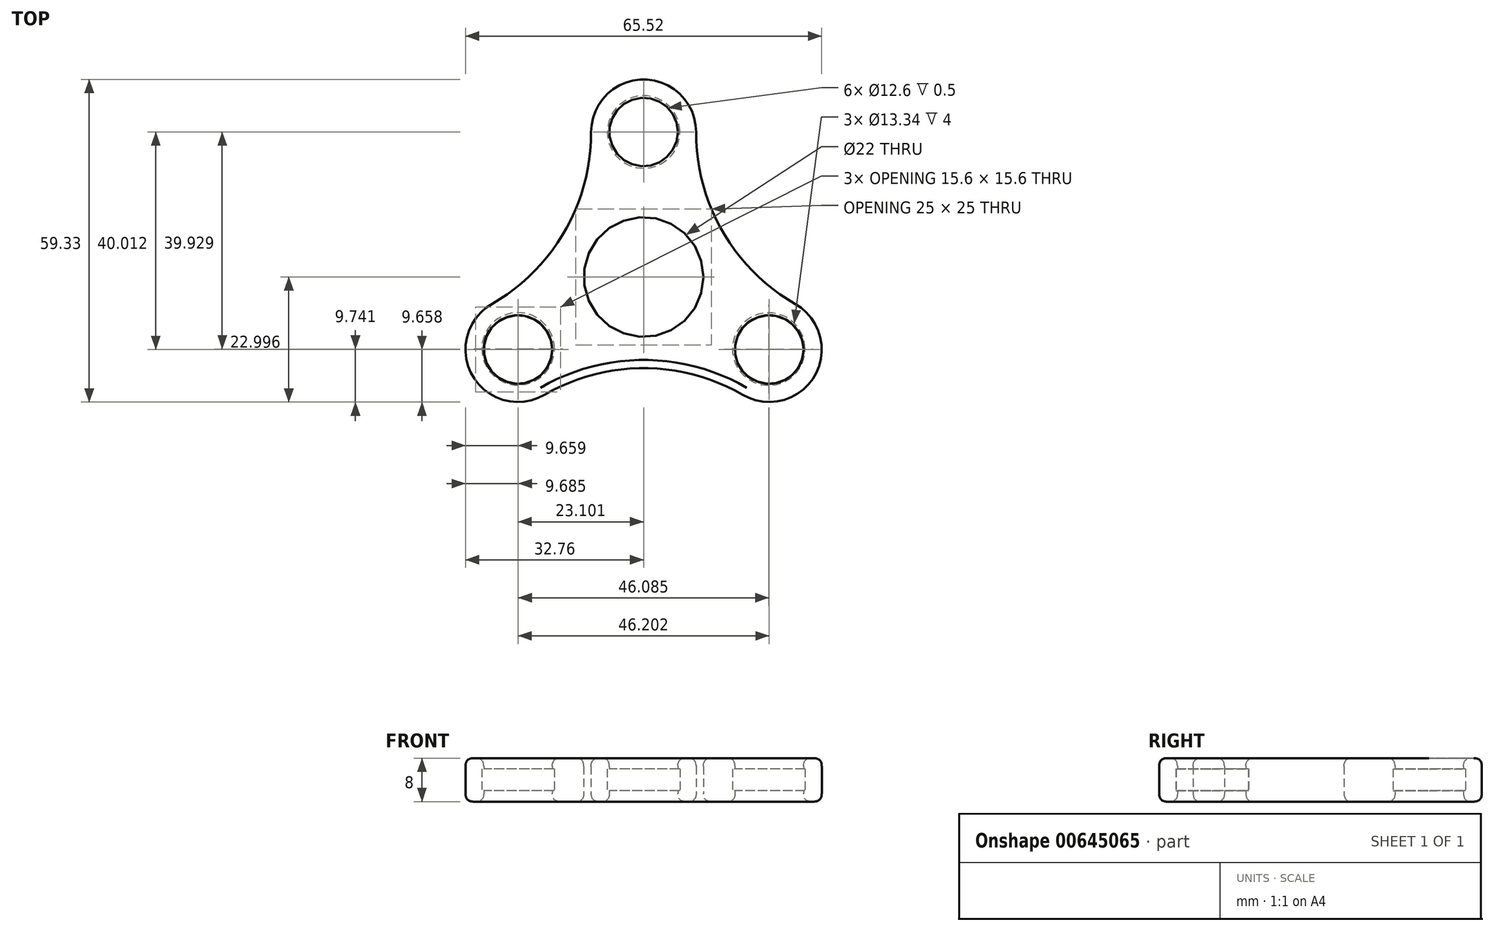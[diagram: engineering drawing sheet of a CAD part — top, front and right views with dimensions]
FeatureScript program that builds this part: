
annotation { "Feature Type Name" : "Feature", "Feature Type Description" : "" }
export const myFeature = defineFeature(function(context is Context, id is Id, definition is map)
    precondition{}
    {
        {
            var Q0;
            Q0=qCreatedBy(makeId("Top.planeOp"),FACE);
            var sketch = newSketch(context, id + "F0", { "sketchPlane" : qUnion([Q0])});
            skCircle(sketch, "E0", {"center": v(0, 0) * mm, "radius": 6.3 * mm});
            skCircle(sketch, "E1", {"center": v(0, 0) * mm, "radius": 9.66 * mm});
            skCircle(sketch, "E2.1.0", {"center": v(-23.1, -40.01) * mm, "radius": 9.66 * mm});
            skCircle(sketch, "E2.1.1", {"center": v(-23.1, -40.01) * mm, "radius": 6.3 * mm});
            skCircle(sketch, "E2.2.0", {"center": v(23.1, -40.01) * mm, "radius": 9.66 * mm});
            skCircle(sketch, "E2.2.1", {"center": v(23.1, -40.01) * mm, "radius": 6.3 * mm});
            skPoint(sketch, "E2.center", {"position": v(0, -26.67) * mm});
            skLineSegment(sketch, "E3", {"start": v(0, 0) * mm, "end": v(-9.66, 0) * mm, "construction": true});
            skCircle(sketch, "E4", {"center": v(0, -26.67) * mm, "radius": 11 * mm});
            skLineSegment(sketch, "E5", {"start": v(0, -26.67) * mm, "end": v(-23.1, -40.01) * mm, "construction": true});
            skLineSegment(sketch, "E6", {"start": v(23.1, -40.01) * mm, "end": v(0, -26.67) * mm, "construction": true});
            skLineSegment(sketch, "E7", {"start": v(0, -26.67) * mm, "end": v(0, 0) * mm, "construction": true});
            skLineSegment(sketch, "E8", {"start": v(23.1, -40.01) * mm, "end": v(27.93, -31.64) * mm, "construction": true});
            skLineSegment(sketch, "E9", {"start": v(0, 0) * mm, "end": v(9.66, 0) * mm, "construction": true});
            skLineSegment(sketch, "E10", {"start": v(-23.1, -40.01) * mm, "end": v(-27.93, -31.64) * mm, "construction": true});
            skArc(sketch, "E11", {"start": v(-27.93, -31.64) * mm, "mid": v(-14.5, -18.3) * mm, "end": v(-9.66, 0) * mm});
            skArc(sketch, "E12", {"start": v(9.66, 0) * mm, "mid": v(14.5, -18.3) * mm, "end": v(27.93, -31.64) * mm});
            skLineSegment(sketch, "E13", {"start": v(-23.1, -40.01) * mm, "end": v(-18.27, -48.38) * mm, "construction": true});
            skLineSegment(sketch, "E14", {"start": v(23.1, -40.01) * mm, "end": v(18.27, -48.38) * mm, "construction": true});
            skArc(sketch, "E15", {"start": v(18.27, -48.38) * mm, "mid": v(0, -43.43) * mm, "end": v(-18.27, -48.38) * mm});
            skSolve(sketch);
        }
        {
            var Q0;
            Q0 = qSketchRegion(id + "F0", true);
            extrude(context, id + "F1", {"entities" : qUnion([Q0]), "depth" : 8 * mm, "offsetDistance" : 25 * mm});
        }
        {
            var Q0;
            Q0=makeQuery(id+"F1.opExtrude","CAP_FACE",FACE,{"disambiguationData":[OSD([sQuery(id+"F0.wireOp",EDGE,"E0"),sQuery(id+"F0.wireOp",EDGE,"E1"),sQuery(id+"F0.wireOp",EDGE,"E2.1.0"),sQuery(id+"F0.wireOp",EDGE,"E2.1.1"),sQuery(id+"F0.wireOp",EDGE,"E2.2.0"),sQuery(id+"F0.wireOp",EDGE,"E2.2.1"),sQuery(id+"F0.wireOp",EDGE,"E4"),sQuery(id+"F0.wireOp",EDGE,"E11"),sQuery(id+"F0.wireOp",EDGE,"E12"),sQuery(id+"F0.wireOp",EDGE,"E15")])],"isStart":true});
            fillet(context, id + "F2", {"entities" : qUnion([Q0]), "radius" : 1.5 * mm, "tangentPropagation" : true, "rho" : 0.5, "crossSection" : FilletCrossSection.CONIC, "allowEdgeOverflow" : false});
        }
        {
            var Q0;
            Q0=makeQuery(id+"F1.opExtrude","CAP_FACE",FACE,{"disambiguationData":[OSD([sQuery(id+"F0.wireOp",EDGE,"E0"),sQuery(id+"F0.wireOp",EDGE,"E1"),sQuery(id+"F0.wireOp",EDGE,"E2.1.0"),sQuery(id+"F0.wireOp",EDGE,"E2.1.1"),sQuery(id+"F0.wireOp",EDGE,"E2.2.0"),sQuery(id+"F0.wireOp",EDGE,"E2.2.1"),sQuery(id+"F0.wireOp",EDGE,"E4"),sQuery(id+"F0.wireOp",EDGE,"E11"),sQuery(id+"F0.wireOp",EDGE,"E12"),sQuery(id+"F0.wireOp",EDGE,"E15")])],"isStart":false});
            fillet(context, id + "F3", {"entities" : qUnion([Q0]), "radius" : 1.5 * mm, "tangentPropagation" : true, "rho" : 0.5, "crossSection" : FilletCrossSection.CONIC, "allowEdgeOverflow" : false});
        }
        {
            var Q0;
            Q0=qCreatedBy(makeId("Right.planeOp"),FACE);
            var sketch = newSketch(context, id + "F4", { "sketchPlane" : qUnion([Q0])});
            skLineSegment(sketch, "E16", {"start": v(18.83, 0) * mm, "end": v(18.83, 4) * mm, "construction": true});
            skSolve(sketch);
        }
        {
            var Q0;
            Q0=sQuery(id+"F4.wireOp",EDGE,"E16");
            cPlane(context, id + "F5", {"entities" : qUnion([Q0]), "cplaneType" : CPlaneType.MID_PLANE, "offset" : 25 * mm, "width" : 150 * mm, "height" : 150 * mm});
        }
        {
            var Q0;
            Q0=qCreatedBy(id+"F5.planeOp",FACE);
            var sketch = newSketch(context, id + "F6", { "sketchPlane" : qUnion([Q0])});
            skCircle(sketch, "E17", {"center": v(0, 0) * mm, "radius": 6.67 * mm});
            skCircle(sketch, "E18.1.0", {"center": v(-23.07, -39.9) * mm, "radius": 6.67 * mm});
            skCircle(sketch, "E18.2.0", {"center": v(23.01, -39.93) * mm, "radius": 6.67 * mm});
            skPoint(sketch, "E18.center", {"position": v(-0.02, -26.6) * mm});
            skSolve(sketch);
        }
        {
            var Q0;
            Q0 = qSketchRegion(id + "F6", true);
            extrude(context, id + "F7", {"entities" : qUnion([Q0]), "operationType" : NewBodyOperationType.REMOVE, "depth" : 4 * mm, "offsetDistance" : 25 * mm});
        }
    });
